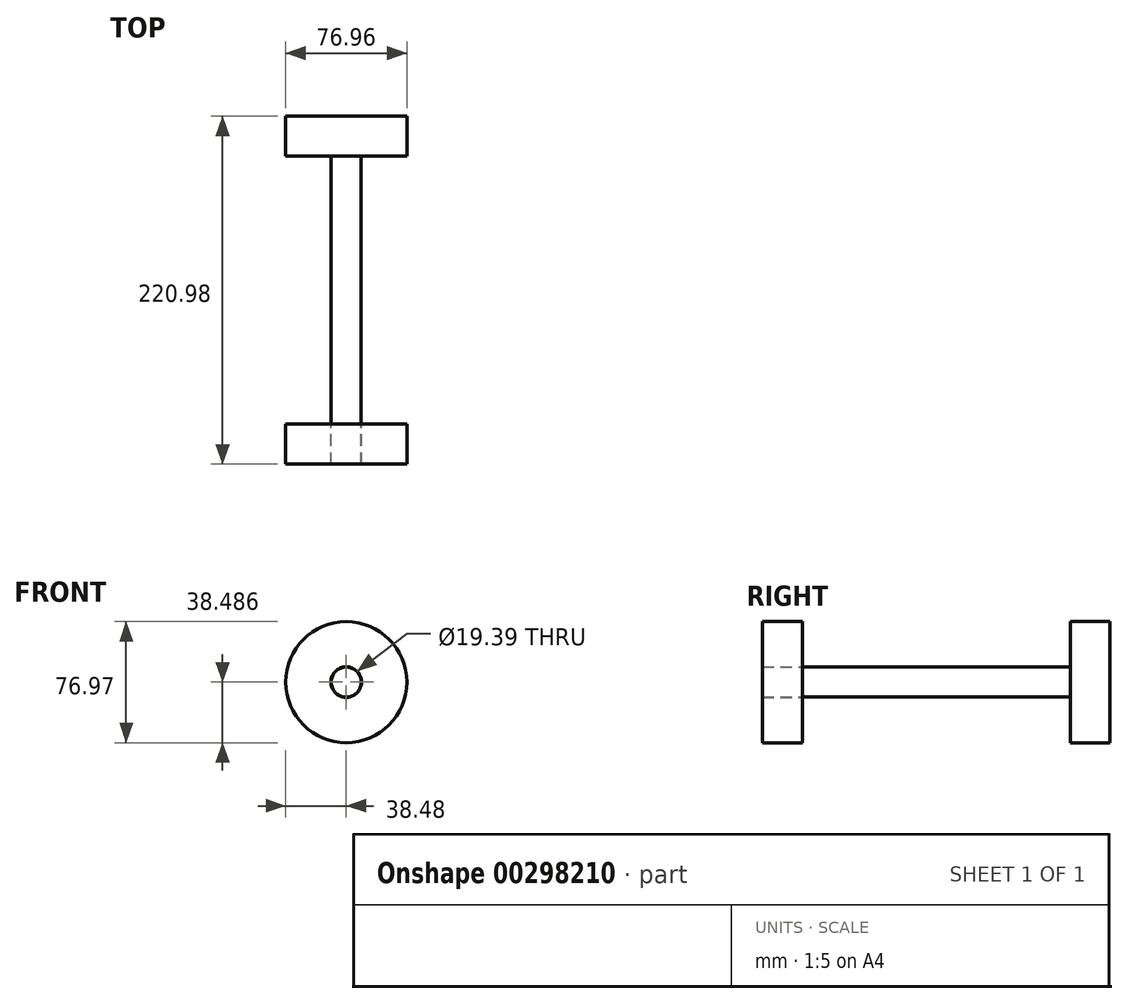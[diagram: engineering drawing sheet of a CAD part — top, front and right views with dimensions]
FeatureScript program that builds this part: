
annotation { "Feature Type Name" : "Feature", "Feature Type Description" : "" }
export const myFeature = defineFeature(function(context is Context, id is Id, definition is map)
    precondition{}
    {
        {
            var Q0;
            Q0=qCreatedBy(makeId("Front.planeOp"),FACE);
            var sketch = newSketch(context, id + "F0", { "sketchPlane" : qUnion([Q0])});
            skCircle(sketch, "E0", {"center": v(0, -3.32) * mm, "radius": 9.53 * mm});
            skSolve(sketch);
        }
        {
            var Q0;
            Q0 = qSketchRegion(id + "F0", true);
            extrude(context, id + "F1", {"entities" : qUnion([Q0]), "depth" : 170.18 * mm});
        }
        {
            var Q0;
            Q0=makeQuery(id+"F1.opExtrude","CAP_FACE",FACE,{"disambiguationData":[OSD([sQuery(id+"F0.wireOp",EDGE,"E0")])],"isStart":false});
            var sketch = newSketch(context, id + "F2", { "sketchPlane" : qUnion([Q0])});
            skCircle(sketch, "E1", {"center": v(0, -3.32) * mm, "radius": 38.48 * mm});
            skCircle(sketch, "E2", {"center": v(0, -3.32) * mm, "radius": 38.5 * mm});
            skCircle(sketch, "E3", {"center": v(0, -3.32) * mm, "radius": 9.7 * mm});
            skCircle(sketch, "E4", {"center": v(0, -3.32) * mm, "radius": 9.55 * mm});
            skSolve(sketch);
        }
        {
            var Q0;
            Q0=makeQuery(id+"F1.opExtrude","CAP_FACE",FACE,{"disambiguationData":[OSD([sQuery(id+"F0.wireOp",EDGE,"E0")])],"isStart":true});
            var sketch = newSketch(context, id + "F3", { "sketchPlane" : qUnion([Q0])});
            skCircle(sketch, "E5", {"center": v(0, -3.32) * mm, "radius": 38.46 * mm});
            skSolve(sketch);
        }
        {
            var Q0;
            Q0 = qSketchRegion(id + "F3", true);
            extrude(context, id + "F4", {"entities" : qUnion([Q0]), "operationType" : NewBodyOperationType.ADD, "depth" : 25.4 * mm});
        }
        {
            var Q0;
            Q0=makeQuery(id+"F2.imprint","IMPRINT",FACE,{"disambiguationData":[TD([[makeQuery(id+"F2.imprint","IMPRINT",EDGE,{"derivedFrom":sQuery(id+"F2.wireOp",EDGE,"E1")}),1.0]])]});
            extrude(context, id + "F5", {"entities" : qUnion([Q0]), "depth" : 25.4 * mm});
        }
        {
            var Q0;
            Q0=makeQuery(id+"F1.opExtrude","CAP_FACE",FACE,{"disambiguationData":[OSD([sQuery(id+"F0.wireOp",EDGE,"E0")])],"isStart":false});
            extrude(context, id + "F6", {"entities" : qUnion([Q0]), "operationType" : NewBodyOperationType.ADD, "depth" : 25.4 * mm});
        }
    });
